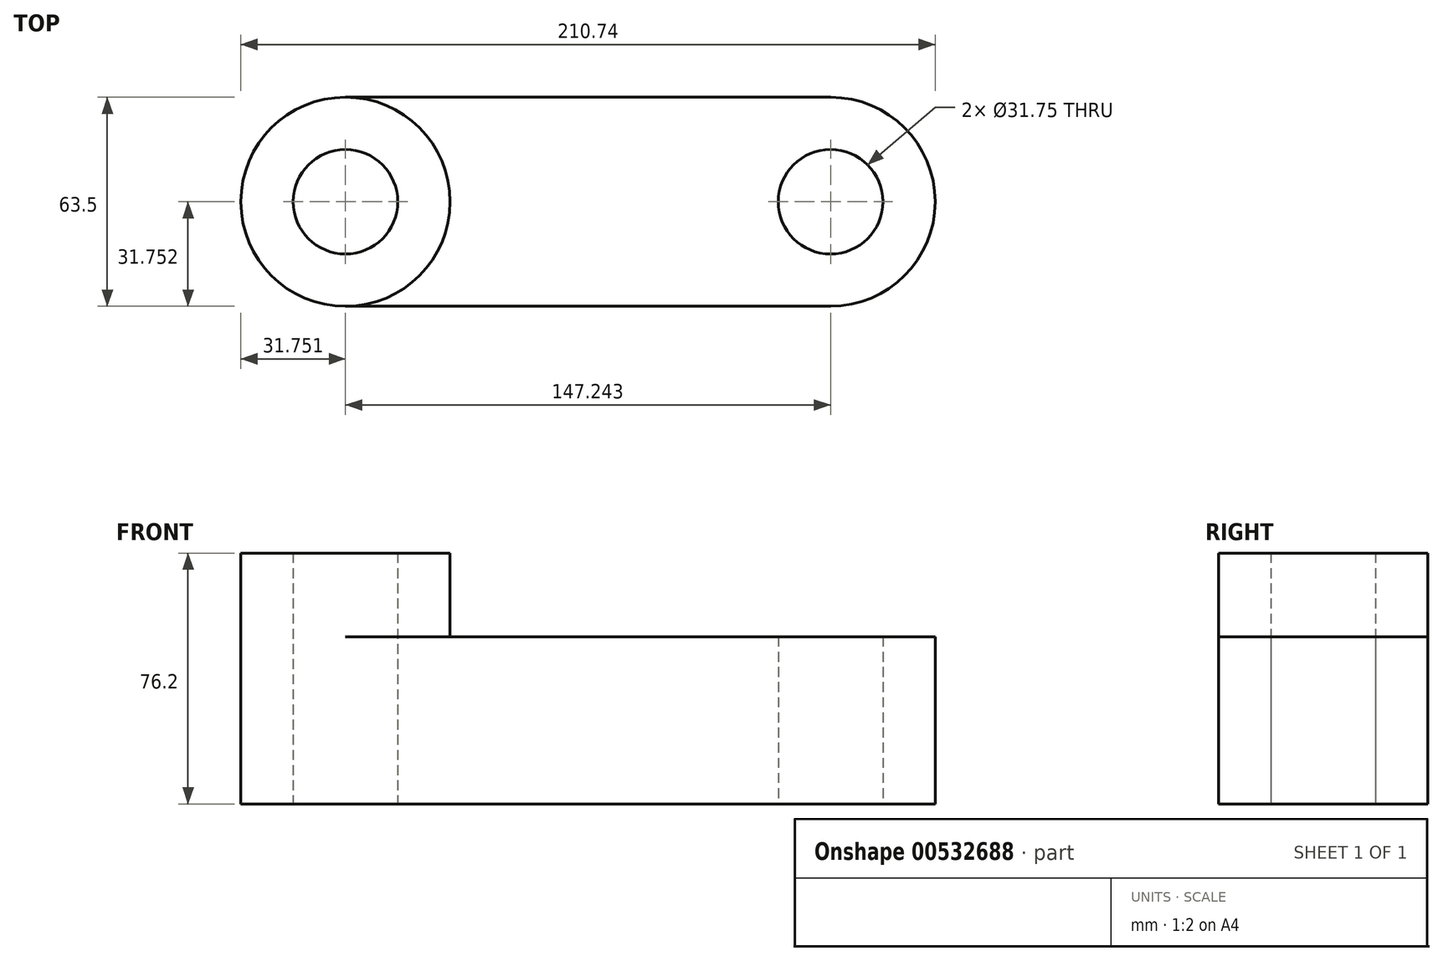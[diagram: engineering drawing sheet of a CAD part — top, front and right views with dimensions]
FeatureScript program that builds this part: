
annotation { "Feature Type Name" : "Feature", "Feature Type Description" : "" }
export const myFeature = defineFeature(function(context is Context, id is Id, definition is map)
    precondition{}
    {
        {
            var Q0;
            Q0=qCreatedBy(makeId("Top.planeOp"),FACE);
            var sketch = newSketch(context, id + "F0", { "sketchPlane" : qUnion([Q0])});
            skLineSegment(sketch, "E0.bottom", {"start": v(-84.86, 36.4) * mm, "end": v(-11.24, 36.4) * mm});
            skLineSegment(sketch, "E0.top", {"start": v(-84.86, -27.1) * mm, "end": v(-11.24, -27.1) * mm});
            skCircle(sketch, "E1", {"center": v(-84.86, 4.65) * mm, "radius": 31.75 * mm});
            skCircle(sketch, "E2", {"center": v(-84.86, 4.65) * mm, "radius": 15.88 * mm});
            skArc(sketch, "E3.MirrorC", {"start": v(62.38, 36.4) * mm, "mid": v(94.13, 4.65) * mm, "end": v(62.38, -27.1) * mm});
            skCircle(sketch, "E4.MirrorC", {"center": v(62.38, 4.65) * mm, "radius": 15.88 * mm});
            skLineSegment(sketch, "E5.MirrorCS", {"start": v(62.38, 36.4) * mm, "end": v(-11.24, 36.4) * mm});
            skLineSegment(sketch, "E6.MirrorCS", {"start": v(62.38, -27.1) * mm, "end": v(-11.24, -27.1) * mm});
            skSolve(sketch);
        }
        {
            var Q0;
            {var subQ1=sQuery(id+"F0.wireOp",EDGE,"E0.bottom");Q0=makeQuery(id+"F0.imprint","IMPRINT",FACE,{"disambiguationData":[TD([[makeQuery(id+"F0.imprint","IMPRINT",EDGE,{"derivedFrom":subQ1}),-1.0]])]});}
            extrude(context, id + "F1", {"entities" : qUnion([Q0]), "depth" : 50.8 * mm, "offsetDistance" : 25.4 * mm});
        }
        {
            var Q0;
            Q0=makeQuery(id+"F0.imprint","IMPRINT",FACE,{"disambiguationData":[TD([[makeQuery(id+"F0.imprint","IMPRINT",EDGE,{"derivedFrom":sQuery(id+"F0.wireOp",EDGE,"E2")}),-1.0]])]});
            extrude(context, id + "F2", {"entities" : qUnion([Q0]), "operationType" : NewBodyOperationType.ADD, "depth" : 76.2 * mm, "offsetDistance" : 25.4 * mm});
        }
    });
